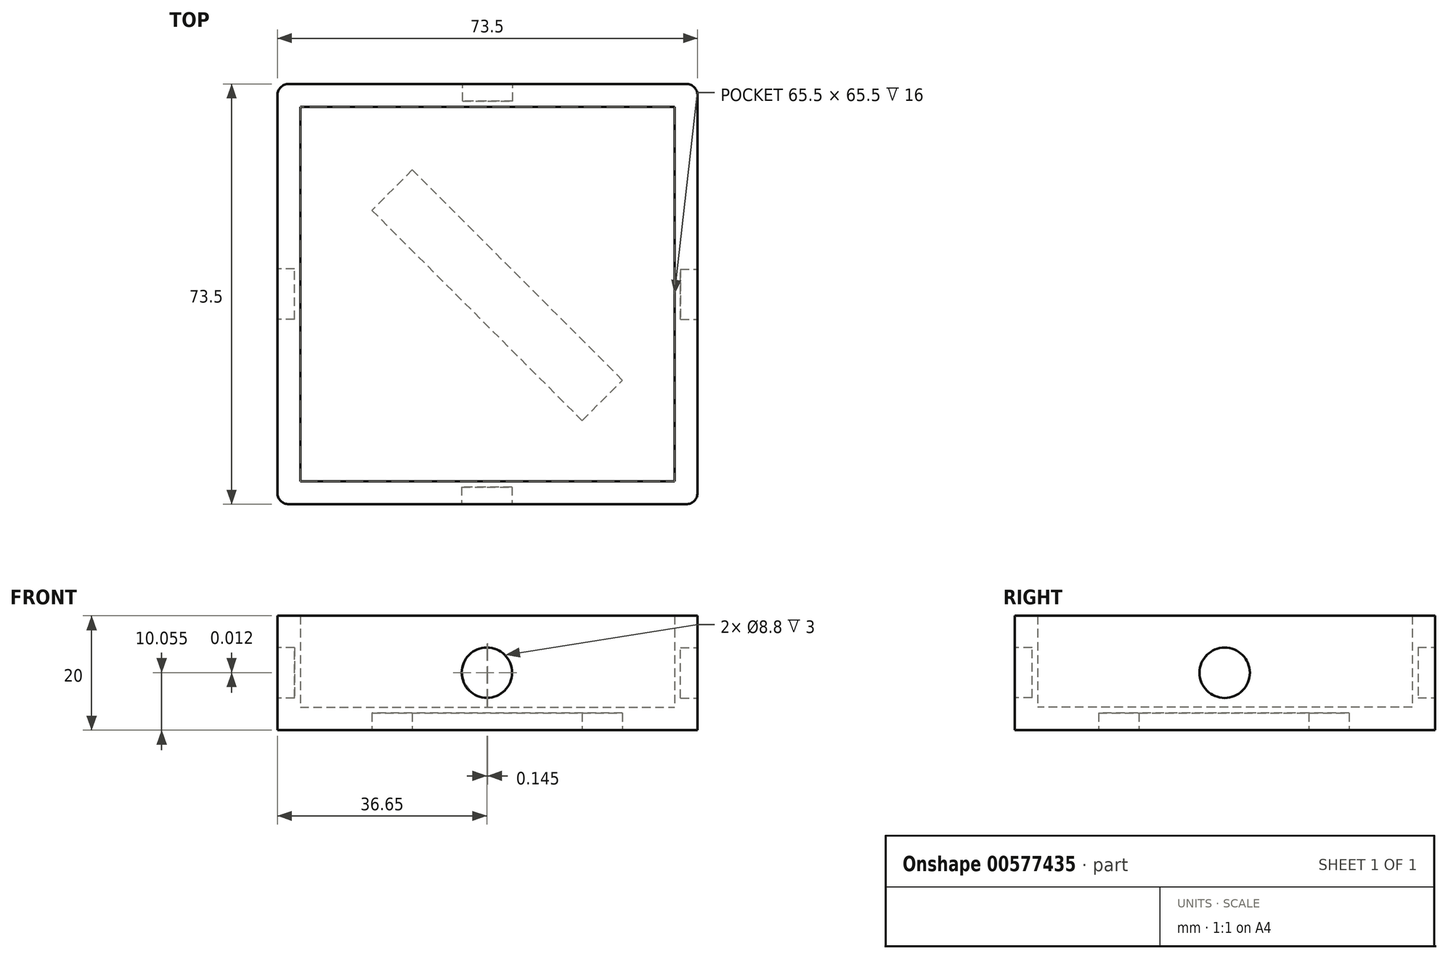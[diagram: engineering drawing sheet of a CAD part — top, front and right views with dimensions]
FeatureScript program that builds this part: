
annotation { "Feature Type Name" : "Feature", "Feature Type Description" : "" }
export const myFeature = defineFeature(function(context is Context, id is Id, definition is map)
    precondition{}
    {
        {
            var Q0;
            Q0=qCreatedBy(makeId("Top.planeOp"),FACE);
            var sketch = newSketch(context, id + "F0", { "sketchPlane" : qUnion([Q0])});
            skLineSegment(sketch, "E0.bottom", {"start": v(-28.45, 28.87) * mm, "end": v(37.05, 28.87) * mm});
            skLineSegment(sketch, "E0.top", {"start": v(-28.45, -36.63) * mm, "end": v(37.05, -36.63) * mm});
            skLineSegment(sketch, "E0.left", {"start": v(-28.45, 28.87) * mm, "end": v(-28.45, -36.63) * mm});
            skLineSegment(sketch, "E0.right", {"start": v(37.05, 28.87) * mm, "end": v(37.05, -36.63) * mm});
            skSolve(sketch);
        }
        {
            var Q0;
            Q0=makeQuery(id+"F0.imprint","IMPRINT",FACE,{"disambiguationData":[TD([[makeQuery(id+"F0.imprint","IMPRINT",EDGE,{"derivedFrom":sQuery(id+"F0.wireOp",EDGE,"E0.bottom")}),-1.0]])]});
            extrude(context, id + "F1", {"entities" : qUnion([Q0]), "depth" : 16 * mm, "offsetDistance" : 25 * mm});
        }
        {
            var Q0;
            Q0=makeQuery(id+"F1.opExtrude","CAP_FACE",FACE,{"disambiguationData":[OSD([sQuery(id+"F0.wireOp",EDGE,"E0.bottom"),sQuery(id+"F0.wireOp",EDGE,"E0.top"),sQuery(id+"F0.wireOp",EDGE,"E0.left"),sQuery(id+"F0.wireOp",EDGE,"E0.right")])],"isStart":false});
            shell(context, id + "F2", {"entities" : qUnion([Q0]), "thickness" : 4 * mm, "oppositeDirection" : true});
        }
        {
            var Q0;
            Q0=makeQuery(id+"F1.opExtrude","SWEPT_EDGE",EDGE,{"disambiguationData":[OSD([sQuery(id+"F0.wireOp",EDGE,"E0.bottom"),sQuery(id+"F0.wireOp",EDGE,"E0.left")])]});
            var Q1;
            Q1=makeQuery(id+"F1.opExtrude","SWEPT_EDGE",EDGE,{"disambiguationData":[OSD([sQuery(id+"F0.wireOp",EDGE,"E0.top"),sQuery(id+"F0.wireOp",EDGE,"E0.left")])]});
            var Q2;
            Q2=makeQuery(id+"F1.opExtrude","SWEPT_EDGE",EDGE,{"disambiguationData":[OSD([sQuery(id+"F0.wireOp",EDGE,"E0.top"),sQuery(id+"F0.wireOp",EDGE,"E0.right")])]});
            var Q3;
            Q3=makeQuery(id+"F1.opExtrude","SWEPT_EDGE",EDGE,{"disambiguationData":[OSD([sQuery(id+"F0.wireOp",EDGE,"E0.bottom"),sQuery(id+"F0.wireOp",EDGE,"E0.right")])]});
            fillet(context, id + "F3", {"entities" : qUnion([Q0, Q1, Q2, Q3]), "radius" : 2 * mm, "tangentPropagation" : true, "allowEdgeOverflow" : false});
        }
        {
            var Q0;
            Q0=makeQuery(id+"F1.opExtrude","SWEPT_FACE",FACE,{"disambiguationData":[OSD([sQuery(id+"F0.wireOp",EDGE,"E0.left")])]});
            var sketch = newSketch(context, id + "F4", { "sketchPlane" : qUnion([Q0])});
            skLineSegment(sketch, "E1", {"start": v(3.88, 16) * mm, "end": v(3.88, -4) * mm, "construction": true});
            skCircle(sketch, "E2", {"center": v(3.88, 6) * mm, "radius": 4.4 * mm});
            skLineSegment(sketch, "E3", {"start": v(38.63, 6) * mm, "end": v(-30.87, 6) * mm, "construction": true});
            skSolve(sketch);
        }
        {
            var Q0;
            Q0=makeQuery(id+"F1.opExtrude","SWEPT_FACE",FACE,{"disambiguationData":[OSD([sQuery(id+"F0.wireOp",EDGE,"E0.top")])]});
            var sketch = newSketch(context, id + "F5", { "sketchPlane" : qUnion([Q0])});
            skCircle(sketch, "E4", {"center": v(4.2, 6.05) * mm, "radius": 4.4 * mm});
            skLineSegment(sketch, "E5", {"start": v(-30.45, 6) * mm, "end": v(39.05, 6) * mm, "construction": true});
            skLineSegment(sketch, "E6", {"start": v(4.3, 16) * mm, "end": v(4.3, -4) * mm, "construction": true});
            skSolve(sketch);
        }
        {
            var Q0;
            Q0=makeQuery(id+"F1.opExtrude","SWEPT_FACE",FACE,{"disambiguationData":[OSD([sQuery(id+"F0.wireOp",EDGE,"E0.right")])]});
            var sketch = newSketch(context, id + "F6", { "sketchPlane" : qUnion([Q0])});
            skCircle(sketch, "E7", {"center": v(-3.93, 6.02) * mm, "radius": 4.4 * mm});
            skSolve(sketch);
        }
        {
            var Q0;
            Q0=makeQuery(id+"F1.opExtrude","SWEPT_FACE",FACE,{"disambiguationData":[OSD([sQuery(id+"F0.wireOp",EDGE,"E0.bottom")])]});
            var sketch = newSketch(context, id + "F7", { "sketchPlane" : qUnion([Q0])});
            skCircle(sketch, "E8", {"center": v(-4.35, 6.07) * mm, "radius": 4.4 * mm});
            skLineSegment(sketch, "E9", {"start": v(30.45, 6) * mm, "end": v(-39.05, 6) * mm, "construction": true});
            skLineSegment(sketch, "E10", {"start": v(-4.3, 16) * mm, "end": v(-4.3, -4) * mm, "construction": true});
            skSolve(sketch);
        }
        {
            var Q0;
            Q0=qSketchRegion(id+"F4",true);
            extrude(context, id + "F8", {"entities" : qUnion([Q0]), "operationType" : NewBodyOperationType.ADD, "oppositeDirection" : true, "depth" : 3 * mm, "offsetDistance" : 25 * mm});
        }
        {
            var Q0;
            Q0=makeQuery(id+"F4.imprint","IMPRINT",FACE,{"disambiguationData":[TD([[makeQuery(id+"F4.imprint","IMPRINT",EDGE,{"derivedFrom":sQuery(id+"F4.wireOp",EDGE,"E2")}),1.0]])]});
            var Q1;
            Q1=sQuery(id+"F4.wireOp",EDGE,"E2");
            extrude(context, id + "F9", {"entities" : qUnion([Q0]), "operationType" : NewBodyOperationType.REMOVE, "surfaceEntities" : qUnion([Q1]), "oppositeDirection" : true, "depth" : 3 * mm, "offsetDistance" : 25 * mm});
        }
        {
            var Q0;
            Q0=makeQuery(id+"F5.imprint","IMPRINT",FACE,{"disambiguationData":[TD([[makeQuery(id+"F5.imprint","IMPRINT",EDGE,{"derivedFrom":sQuery(id+"F5.wireOp",EDGE,"E4")}),1.0]])]});
            var Q1;
            Q1=sQuery(id+"F5.wireOp",EDGE,"E4");
            extrude(context, id + "F10", {"entities" : qUnion([Q0]), "operationType" : NewBodyOperationType.REMOVE, "surfaceEntities" : qUnion([Q1]), "oppositeDirection" : true, "depth" : 3 * mm, "offsetDistance" : 25 * mm});
        }
        {
            var Q0;
            Q0=makeQuery(id+"F6.imprint","IMPRINT",FACE,{"disambiguationData":[TD([[makeQuery(id+"F6.imprint","IMPRINT",EDGE,{"derivedFrom":sQuery(id+"F6.wireOp",EDGE,"E7")}),1.0]])]});
            extrude(context, id + "F11", {"entities" : qUnion([Q0]), "operationType" : NewBodyOperationType.REMOVE, "oppositeDirection" : true, "depth" : 3 * mm, "offsetDistance" : 25 * mm});
        }
        {
            var Q0;
            Q0=makeQuery(id+"F7.imprint","IMPRINT",FACE,{"disambiguationData":[TD([[makeQuery(id+"F7.imprint","IMPRINT",EDGE,{"derivedFrom":sQuery(id+"F7.wireOp",EDGE,"E8")}),1.0]])]});
            extrude(context, id + "F12", {"entities" : qUnion([Q0]), "operationType" : NewBodyOperationType.REMOVE, "oppositeDirection" : true, "depth" : 3 * mm, "offsetDistance" : 25 * mm});
        }
        {
            var Q0;
            Q0=makeQuery(id+"F1.opExtrude","CAP_FACE",FACE,{"disambiguationData":[OSD([sQuery(id+"F0.wireOp",EDGE,"E0.bottom"),sQuery(id+"F0.wireOp",EDGE,"E0.top"),sQuery(id+"F0.wireOp",EDGE,"E0.left"),sQuery(id+"F0.wireOp",EDGE,"E0.right")])],"isStart":true});
            var sketch = newSketch(context, id + "F13", { "sketchPlane" : qUnion([Q0])});
            skLineSegment(sketch, "E11", {"start": v(20.85, 26) * mm, "end": v(27.93, 18.94) * mm});
            skLineSegment(sketch, "E12", {"start": v(27.93, 18.94) * mm, "end": v(-8.84, -17.83) * mm});
            skLineSegment(sketch, "E13", {"start": v(-8.84, -17.83) * mm, "end": v(-15.91, -10.77) * mm});
            skLineSegment(sketch, "E14", {"start": v(-15.91, -10.77) * mm, "end": v(20.85, 26) * mm});
            skSolve(sketch);
        }
        {
            var Q0;
            Q0=makeQuery(id+"F13.imprint","IMPRINT",FACE,{"disambiguationData":[TD([[makeQuery(id+"F13.imprint","IMPRINT",EDGE,{"derivedFrom":sQuery(id+"F13.wireOp",EDGE,"E11")}),-1.0]])]});
            extrude(context, id + "F14", {"entities" : qUnion([Q0]), "operationType" : NewBodyOperationType.REMOVE, "oppositeDirection" : true, "depth" : 3 * mm, "offsetDistance" : 25 * mm});
        }
    });
